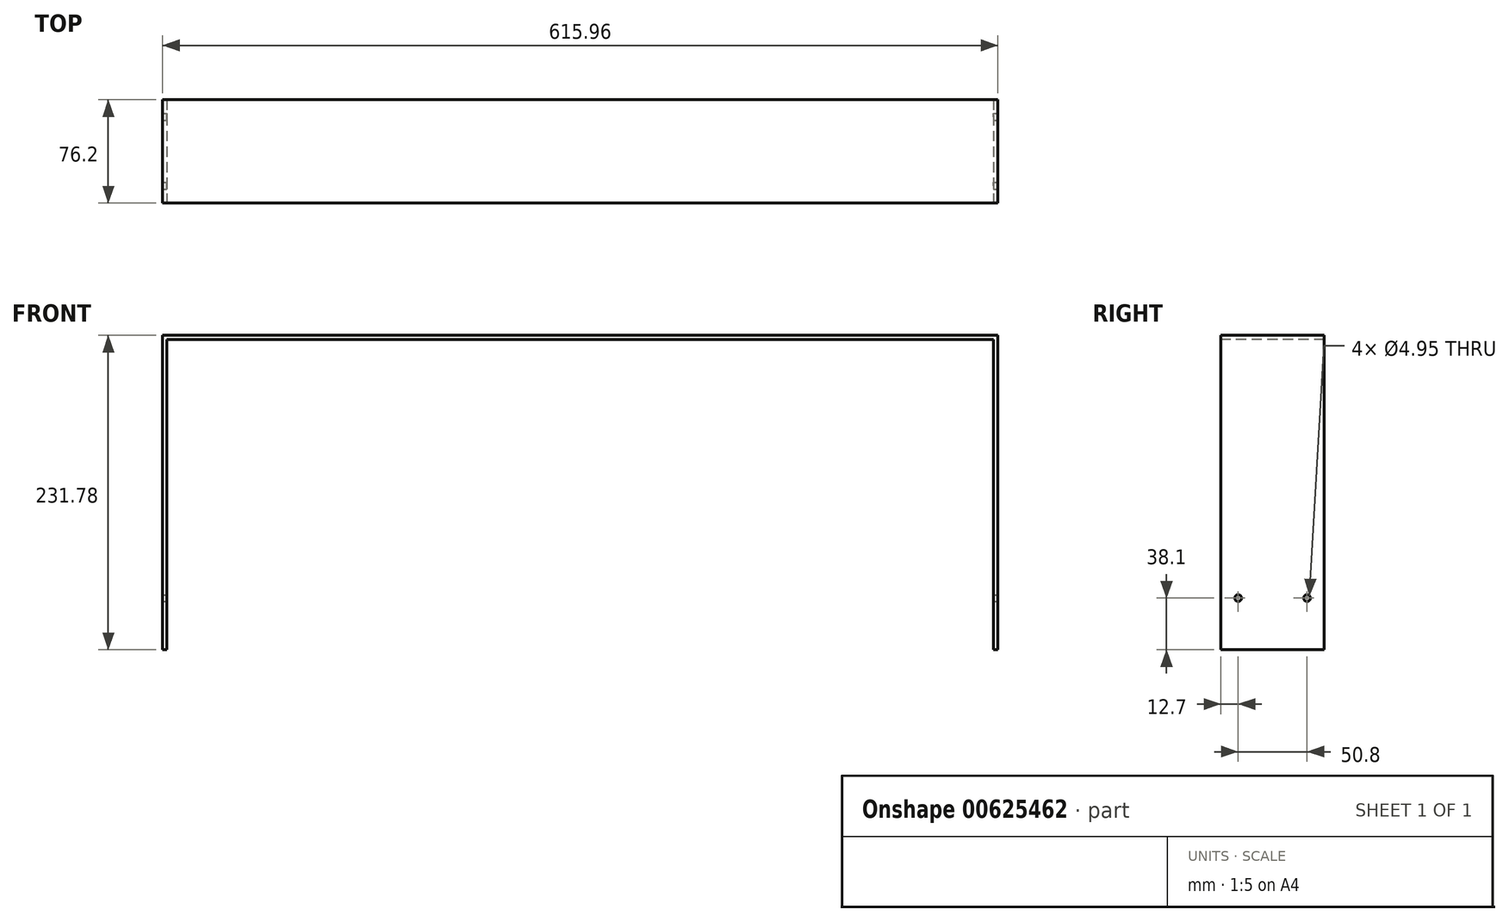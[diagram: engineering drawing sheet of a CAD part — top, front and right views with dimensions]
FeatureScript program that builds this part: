
annotation { "Feature Type Name" : "Feature", "Feature Type Description" : "" }
export const myFeature = defineFeature(function(context is Context, id is Id, definition is map)
    precondition{}
    {
        {
            var Q0;
            Q0=qCreatedBy(makeId("Top.planeOp"),FACE);
            var sketch = newSketch(context, id + "F0", { "sketchPlane" : qUnion([Q0])});
            skLineSegment(sketch, "E0.bottom", {"start": v(-307.98, 38.1) * mm, "end": v(307.97, 38.1) * mm});
            skLineSegment(sketch, "E0.top", {"start": v(-307.98, -38.1) * mm, "end": v(307.97, -38.1) * mm});
            skLineSegment(sketch, "E0.left", {"start": v(-307.98, 38.1) * mm, "end": v(-307.98, -38.1) * mm});
            skLineSegment(sketch, "E0.right", {"start": v(307.97, 38.1) * mm, "end": v(307.97, -38.1) * mm});
            skPoint(sketch, "E0.middle", {"position": v(0, 0) * mm});
            skSolve(sketch);
        }
        {
            var Q0;
            Q0 = qSketchRegion(id + "F0", true);
            extrude(context, id + "F1", {"entities" : qUnion([Q0]), "depth" : 231.77 * mm, "offsetDistance" : 25.4 * mm});
        }
        {
            var Q0;
            Q0=makeQuery(id+"F1.opExtrude","SWEPT_FACE",FACE,{"disambiguationData":[OSD([sQuery(id+"F0.wireOp",EDGE,"E0.top")])]});
            var sketch = newSketch(context, id + "F2", { "sketchPlane" : qUnion([Q0])});
            skLineSegment(sketch, "E1", {"start": v(-307.98, 0) * mm, "end": v(-307.98, 231.78) * mm});
            skLineSegment(sketch, "E2", {"start": v(-307.98, 231.78) * mm, "end": v(307.97, 231.78) * mm});
            skLineSegment(sketch, "E3", {"start": v(307.97, 231.78) * mm, "end": v(307.97, 0) * mm});
            skLineSegment(sketch, "E4.0", {"start": v(304.8, 228.6) * mm, "end": v(304.8, 0) * mm});
            skLineSegment(sketch, "E4.1", {"start": v(-304.8, 228.6) * mm, "end": v(304.8, 228.6) * mm});
            skLineSegment(sketch, "E4.2", {"start": v(-304.8, 0) * mm, "end": v(-304.8, 228.6) * mm});
            skLineSegment(sketch, "E5", {"start": v(-304.8, 0) * mm, "end": v(304.8, 0) * mm});
            skSolve(sketch);
        }
        {
            var Q0;
            Q0 = qSketchRegion(id + "F2", true);
            extrude(context, id + "F3", {"entities" : qUnion([Q0]), "operationType" : NewBodyOperationType.REMOVE, "endBound" : BoundingType.THROUGH_ALL, "oppositeDirection" : true, "depth" : 25.4 * mm, "offsetDistance" : 25.4 * mm});
        }
        {
            var Q0;
            Q0=makeQuery(id+"F1.opExtrude","SWEPT_FACE",FACE,{"disambiguationData":[OSD([sQuery(id+"F0.wireOp",EDGE,"E0.right")])]});
            var sketch = newSketch(context, id + "F4", { "sketchPlane" : qUnion([Q0])});
            skCircle(sketch, "E6", {"center": v(-25.4, 38.1) * mm, "radius": 2.48 * mm});
            skCircle(sketch, "E7", {"center": v(25.4, 38.1) * mm, "radius": 2.48 * mm});
            skLineSegment(sketch, "E8", {"start": v(-25.4, 38.1) * mm, "end": v(-38.1, 38.1) * mm});
            skLineSegment(sketch, "E9", {"start": v(25.4, 38.1) * mm, "end": v(38.1, 38.1) * mm});
            skSolve(sketch);
        }
        {
            var Q0;
            Q0 = qSketchRegion(id + "F4", true);
            extrude(context, id + "F5", {"entities" : qUnion([Q0]), "operationType" : NewBodyOperationType.REMOVE, "endBound" : BoundingType.THROUGH_ALL, "oppositeDirection" : true, "depth" : 25.4 * mm, "offsetDistance" : 25.4 * mm});
        }
    });
